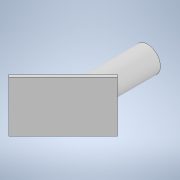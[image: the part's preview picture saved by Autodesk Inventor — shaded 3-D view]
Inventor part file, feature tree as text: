
AUTODESK INVENTOR PART (.ipt)
format: ipt  version: 2020 (Build 240168000, 168)  size: 151,040 bytes
history: native  units: in
note: dims shown in document units (in); Inventor stores cm internally (conversion verified against a paired STEP export)
features: sketch x8, extrude x7, chamfer x1
ambient origin geometry x8: Origin, YZ Plane, XZ Plane, XY Plane, X Axis, Y Axis, Z Axis, Center Point
bodies: Solid1 (feature_tree)
feature tree (16):
  extrude  "Extrusion1"  Depth=5.0in TaperAngle=0.0deg
  extrude  "Extrusion3"  Depth=2.0in TaperAngle=45.0deg
  chamfer  "Chamfer1"  Distance=2.0in
  sketch  "Sketch5"  dims[d12=2.0in d13=0.0in d14=2.0in d15=0.0in]
  extrude  "Extrusion4"  Depth=2.0in TaperAngle=0.0deg
  extrude  "Extrusion5"  Depth=6.0in
  extrude  "Extrusion6"  Depth=0.25in TaperAngle=0.0deg
  extrude  "Extrusion7"  [1 undecoded]
  extrude  "Extrusion8"  [1 undecoded]
  sketch  "Sketch1"  dims[d0=2.0in d1=5.0in d2=0.0in]
  sketch  "Sketch4"  dims[d5=2.0in d6=0.0in d7=2.0in d8=0.125in d9=45.0deg d10=2.0in d11=0.0in]
  sketch  "Sketch6"  dims[d16=2.0in d17=0.0in d18=6.0in]
  sketch  "Sketch7"  dims[d19=4.0in d20=0.25in d21=0.0in]
  sketch  "Sketch8"
  sketch  "Sketch10"
  sketch  "Sketch11"
note: 2 required parameter values undecoded (feature->parameter linkage not recoverable at this tier; creation-order binding heuristic only, values carry confidence <= 0.55)
